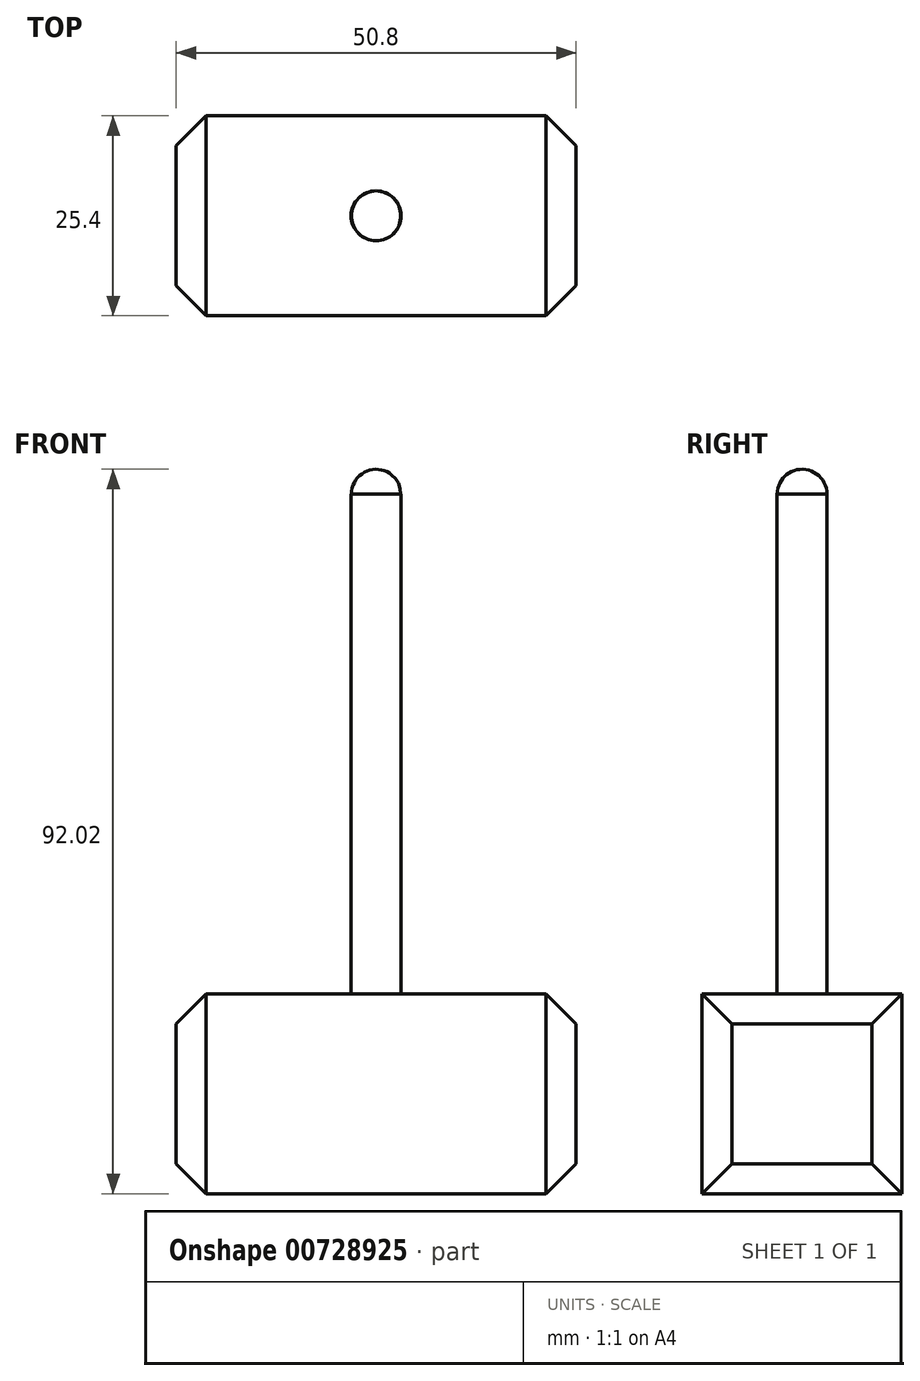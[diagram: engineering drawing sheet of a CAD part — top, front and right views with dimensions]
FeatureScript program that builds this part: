
annotation { "Feature Type Name" : "Feature", "Feature Type Description" : "" }
export const myFeature = defineFeature(function(context is Context, id is Id, definition is map)
    precondition{}
    {
        {
            var Q0;
            Q0=qCreatedBy(makeId("Top.planeOp"),FACE);
            var sketch = newSketch(context, id + "F0", { "sketchPlane" : qUnion([Q0])});
            skLineSegment(sketch, "E0.bottom", {"start": v(25.4, -12.7) * mm, "end": v(-25.4, -12.7) * mm});
            skLineSegment(sketch, "E0.top", {"start": v(25.4, 12.7) * mm, "end": v(-25.4, 12.7) * mm});
            skLineSegment(sketch, "E0.left", {"start": v(25.4, -12.7) * mm, "end": v(25.4, 12.7) * mm});
            skLineSegment(sketch, "E0.right", {"start": v(-25.4, -12.7) * mm, "end": v(-25.4, 12.7) * mm});
            skPoint(sketch, "E0.middle", {"position": v(0, 0) * mm});
            skSolve(sketch);
        }
        {
            var Q0;
            Q0=makeQuery(id+"F0.imprint","IMPRINT",FACE,{"disambiguationData":[TD([[makeQuery(id+"F0.imprint","IMPRINT",EDGE,{"derivedFrom":sQuery(id+"F0.wireOp",EDGE,"E0.bottom")}),-1.0]])]});
            extrude(context, id + "F1", {"entities" : qUnion([Q0]), "depth" : 25.4 * mm, "offsetDistance" : 25.4 * mm});
        }
        {
            var Q0;
            Q0=makeQuery(id+"F1.opExtrude","CAP_FACE",FACE,{"disambiguationData":[OSD([sQuery(id+"F0.wireOp",EDGE,"E0.bottom"),sQuery(id+"F0.wireOp",EDGE,"E0.top"),sQuery(id+"F0.wireOp",EDGE,"E0.left"),sQuery(id+"F0.wireOp",EDGE,"E0.right")])],"isStart":false});
            var sketch = newSketch(context, id + "F2", { "sketchPlane" : qUnion([Q0])});
            skCircle(sketch, "E1", {"center": v(0, 0) * mm, "radius": 3.18 * mm});
            skSolve(sketch);
        }
        {
            var Q0;
            Q0=makeQuery(id+"F2.imprint","IMPRINT",FACE,{"disambiguationData":[TD([[makeQuery(id+"F2.imprint","IMPRINT",EDGE,{"derivedFrom":sQuery(id+"F2.wireOp",EDGE,"E1")}),1.0]])]});
            extrude(context, id + "F3", {"entities" : qUnion([Q0]), "operationType" : NewBodyOperationType.ADD, "depth" : 63.5 * mm, "offsetDistance" : 25.4 * mm});
        }
        {
            var Q0;
            Q0=makeQuery(id+"F3.opExtrude","CAP_FACE",FACE,{"disambiguationData":[OSD([sQuery(id+"F2.wireOp",EDGE,"E1")])],"isStart":false});
            var sketch = newSketch(context, id + "F4", { "sketchPlane" : qUnion([Q0])});
            skArc(sketch, "E2", {"start": v(0, -3.18) * mm, "mid": v(3.12, 0) * mm, "end": v(0, 3.18) * mm});
            skLineSegment(sketch, "E3", {"start": v(0, 3.18) * mm, "end": v(0, -3.18) * mm});
            skSolve(sketch);
        }
        {
            var Q0;
            Q0=makeQuery(id+"F4.imprint","IMPRINT",FACE,{"disambiguationData":[TD([[makeQuery(id+"F4.imprint","IMPRINT",EDGE,{"derivedFrom":sQuery(id+"F4.wireOp",EDGE,"E2")}),1.0]])]});
            var Q1;
            Q1=sQuery(id+"F4.wireOp",EDGE,"E3");
            revolve(context, id + "F5", {"operationType" : NewBodyOperationType.ADD, "surfaceOperationType" : NewSurfaceOperationType.NEW, "entities" : qUnion([Q0]), "axis" : qUnion([Q1]), "revolveType" : RevolveType.FULL});
        }
        {
            var Q0;
            Q0=makeQuery(id+"F1.opExtrude","CAP_EDGE",EDGE,{"disambiguationData":[OSD([sQuery(id+"F0.wireOp",EDGE,"E0.right")])],"isStart":false});
            var Q1;
            Q1=makeQuery(id+"F1.opExtrude","SWEPT_EDGE",EDGE,{"disambiguationData":[OSD([sQuery(id+"F0.wireOp",EDGE,"E0.top"),sQuery(id+"F0.wireOp",EDGE,"E0.right")])]});
            var Q2;
            Q2=makeQuery(id+"F1.opExtrude","CAP_EDGE",EDGE,{"disambiguationData":[OSD([sQuery(id+"F0.wireOp",EDGE,"E0.right")])],"isStart":true});
            var Q3;
            Q3=makeQuery(id+"F1.opExtrude","SWEPT_EDGE",EDGE,{"disambiguationData":[OSD([sQuery(id+"F0.wireOp",EDGE,"E0.bottom"),sQuery(id+"F0.wireOp",EDGE,"E0.right")])]});
            var Q4;
            Q4=makeQuery(id+"F1.opExtrude","CAP_EDGE",EDGE,{"disambiguationData":[OSD([sQuery(id+"F0.wireOp",EDGE,"E0.left")])],"isStart":true});
            var Q5;
            Q5=makeQuery(id+"F1.opExtrude","SWEPT_EDGE",EDGE,{"disambiguationData":[OSD([sQuery(id+"F0.wireOp",EDGE,"E0.bottom"),sQuery(id+"F0.wireOp",EDGE,"E0.left")])]});
            var Q6;
            Q6=makeQuery(id+"F1.opExtrude","SWEPT_FACE",FACE,{"disambiguationData":[OSD([sQuery(id+"F0.wireOp",EDGE,"E0.left")])]});
            chamfer(context, id + "F6", {"entities" : qUnion([Q0, Q1, Q2, Q3, Q4, Q5, Q6]), "width" : 3.8 * mm, "tangentPropagation" : true});
        }
    });
